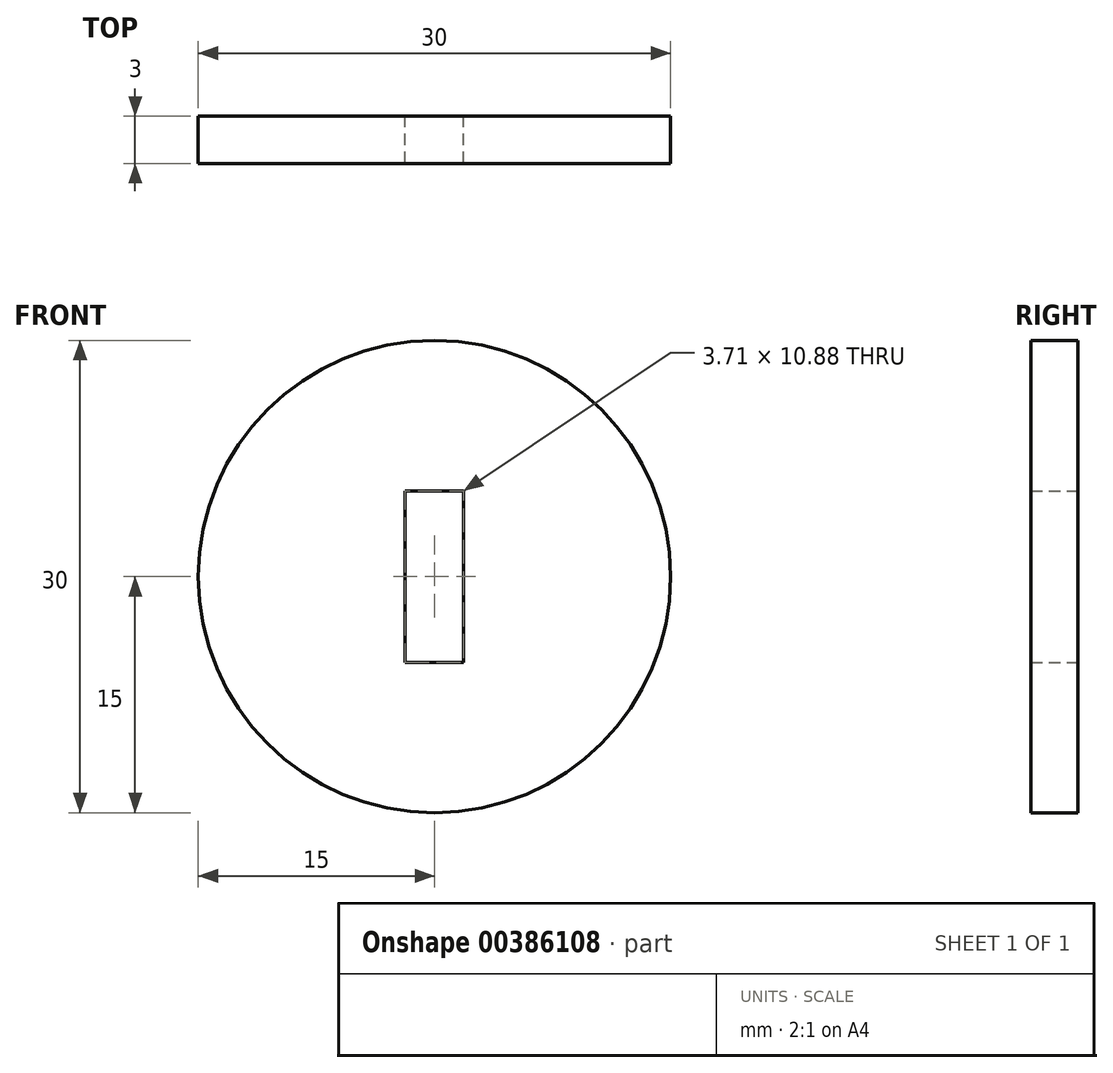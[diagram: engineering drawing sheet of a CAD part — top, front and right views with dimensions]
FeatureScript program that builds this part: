
annotation { "Feature Type Name" : "Feature", "Feature Type Description" : "" }
export const myFeature = defineFeature(function(context is Context, id is Id, definition is map)
    precondition{}
    {
        {
            var Q0;
            Q0=qCreatedBy(makeId("Front.planeOp"),FACE);
            var sketch = newSketch(context, id + "F0", { "sketchPlane" : qUnion([Q0])});
            skCircle(sketch, "E0", {"center": v(0, 0) * mm, "radius": 15 * mm});
            skSolve(sketch);
        }
        {
            var Q0;
            Q0 = qSketchRegion(id + "F0", true);
            extrude(context, id + "F1", {"entities" : qUnion([Q0]), "depth" : 3 * mm});
        }
        {
            var Q0;
            Q0=qCreatedBy(makeId("Front.planeOp"),FACE);
            var sketch = newSketch(context, id + "F2", { "sketchPlane" : qUnion([Q0])});
            skPoint(sketch, "E1.middle", {"position": v(0, 15.1) * mm});
            skPoint(sketch, "E1.top.end.orphan", {"position": v(-1.1, 19.48) * mm});
            skPoint(sketch, "E1.left.end.orphan", {"position": v(1.1, 19.48) * mm});
            skPoint(sketch, "E1.bottom.end.orphan", {"position": v(-1.1, 10.7) * mm});
            skPoint(sketch, "E1.bottom.start.orphan", {"position": v(1.1, 10.7) * mm});
            skLineSegment(sketch, "E2.bottom", {"start": v(-1.86, 5.44) * mm, "end": v(1.86, 5.44) * mm});
            skLineSegment(sketch, "E2.top", {"start": v(-1.86, -5.44) * mm, "end": v(1.86, -5.44) * mm});
            skLineSegment(sketch, "E2.left", {"start": v(-1.86, 5.44) * mm, "end": v(-1.86, -5.44) * mm});
            skLineSegment(sketch, "E2.right", {"start": v(1.86, 5.44) * mm, "end": v(1.86, -5.44) * mm});
            skPoint(sketch, "E2.middle", {"position": v(0, 0) * mm});
            skSolve(sketch);
        }
        {
            var Q0;
            Q0 = qSketchRegion(id + "F2", true);
            extrude(context, id + "F3", {"entities" : qUnion([Q0]), "operationType" : NewBodyOperationType.REMOVE, "depth" : 25 * mm});
        }
    });
